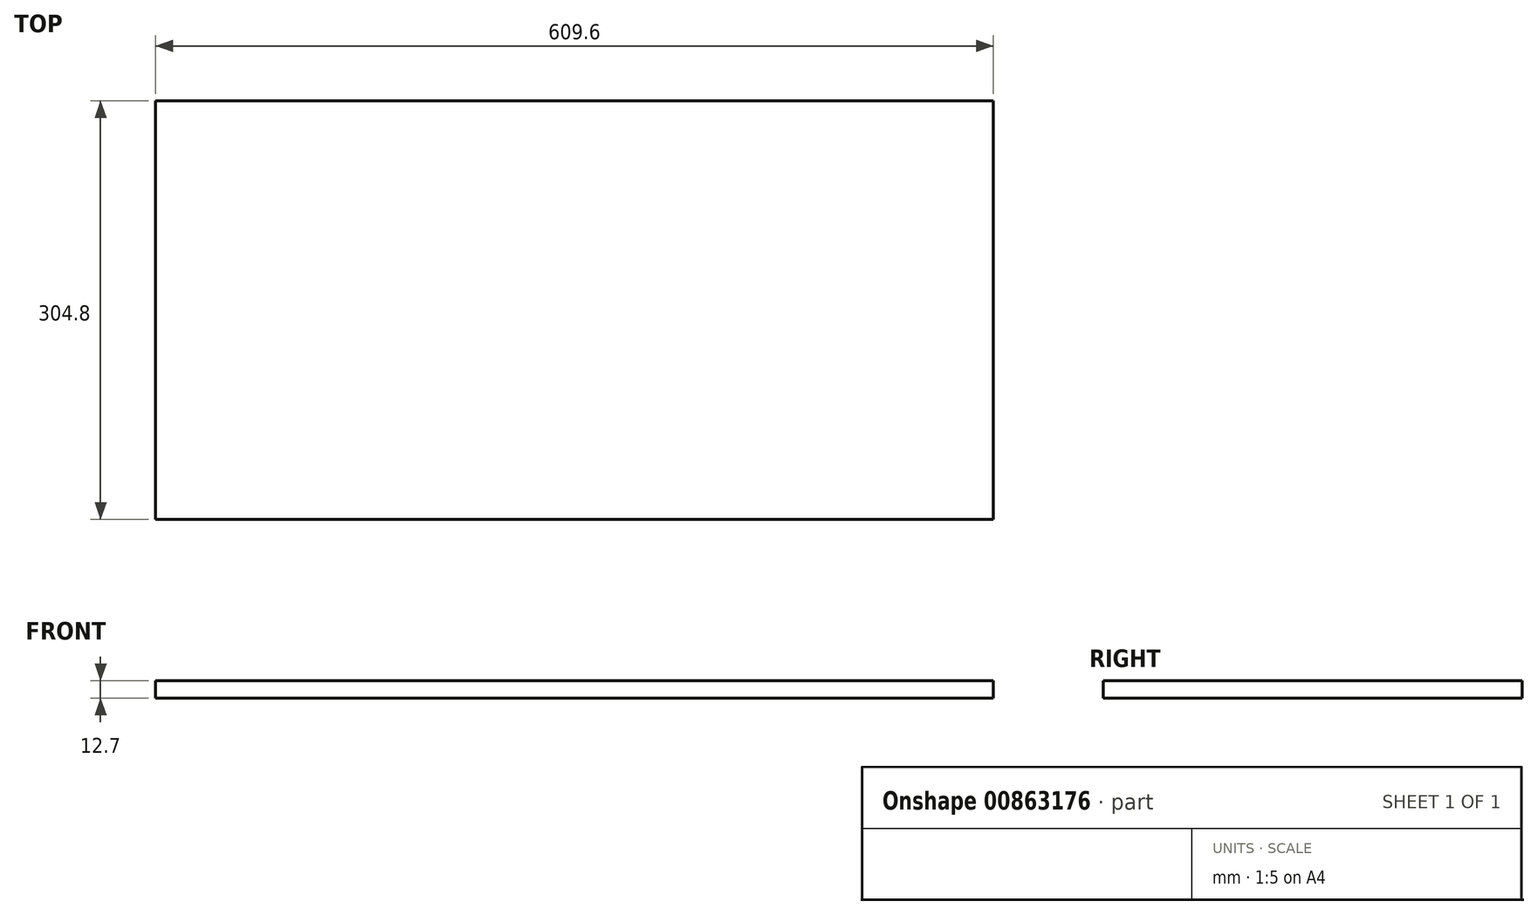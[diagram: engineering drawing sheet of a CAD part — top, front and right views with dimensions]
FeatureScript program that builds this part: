
annotation { "Feature Type Name" : "Feature", "Feature Type Description" : "" }
export const myFeature = defineFeature(function(context is Context, id is Id, definition is map)
    precondition{}
    {
        {
            var Q0;
            Q0=qCreatedBy(makeId("Top.planeOp"),FACE);
            var sketch = newSketch(context, id + "F0", { "sketchPlane" : qUnion([Q0])});
            skLineSegment(sketch, "E0.bottom", {"start": v(304.8, 152.4) * mm, "end": v(-304.8, 152.4) * mm});
            skLineSegment(sketch, "E0.top", {"start": v(304.8, -152.4) * mm, "end": v(-304.8, -152.4) * mm});
            skLineSegment(sketch, "E0.left", {"start": v(304.8, 152.4) * mm, "end": v(304.8, -152.4) * mm});
            skLineSegment(sketch, "E0.right", {"start": v(-304.8, 152.4) * mm, "end": v(-304.8, -152.4) * mm});
            skPoint(sketch, "E0.middle", {"position": v(0, 0) * mm});
            skSolve(sketch);
        }
        {
            var Q0;
            Q0=makeQuery(id+"F0.imprint","IMPRINT",FACE,{"disambiguationData":[TD([[makeQuery(id+"F0.imprint","IMPRINT",EDGE,{"derivedFrom":sQuery(id+"F0.wireOp",EDGE,"E0.bottom")}),1.0]])]});
            extrude(context, id + "F1", {"entities" : qUnion([Q0]), "depth" : 12.7 * mm, "offsetDistance" : 25.4 * mm});
        }
    });
